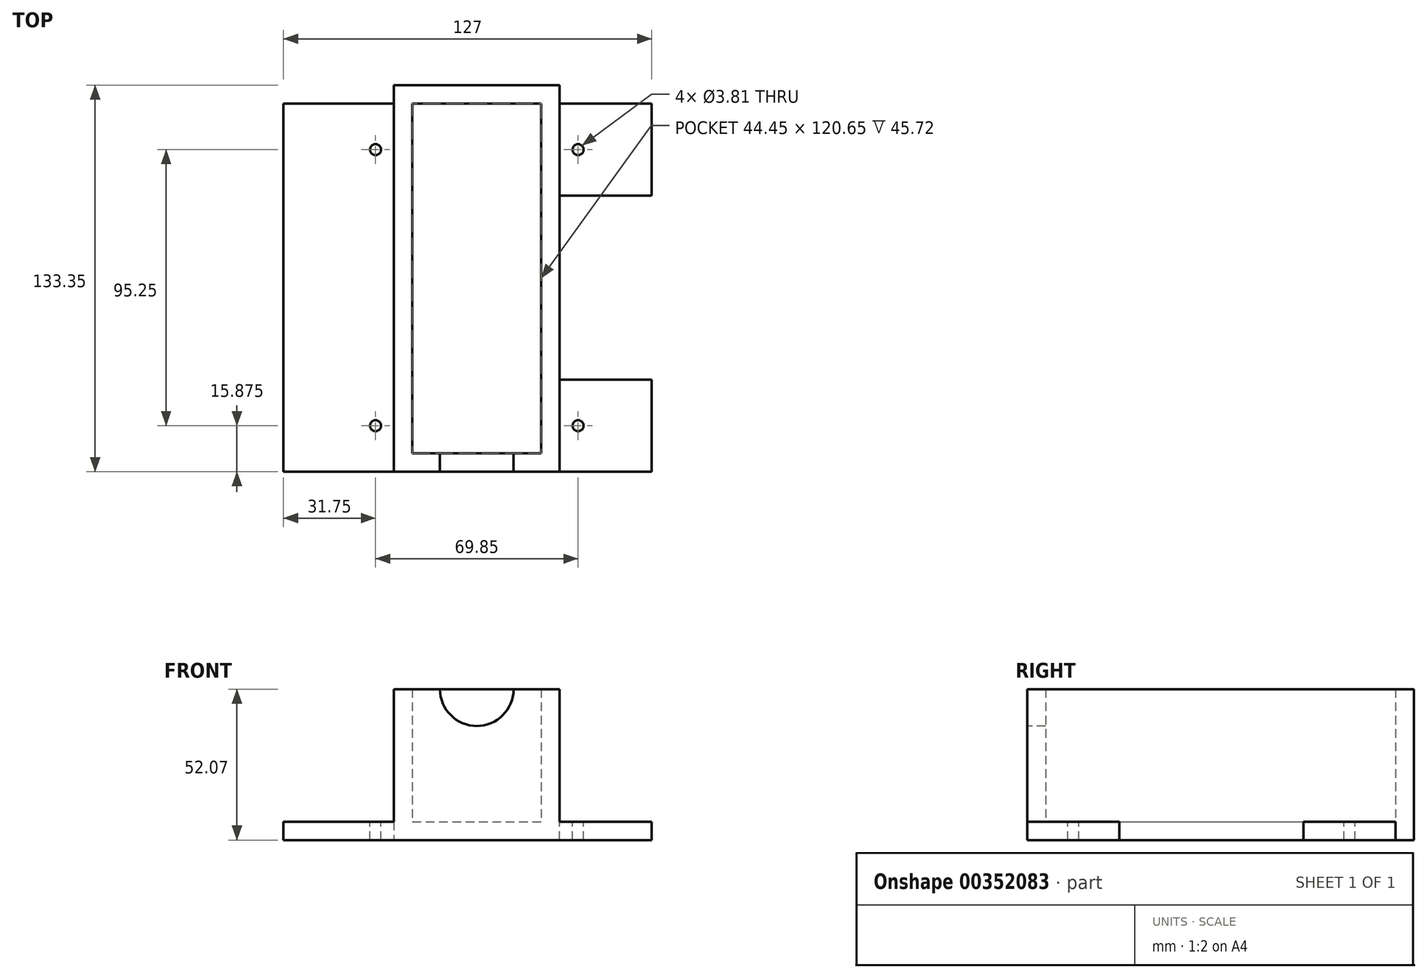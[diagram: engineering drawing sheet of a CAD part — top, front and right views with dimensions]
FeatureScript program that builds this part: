
annotation { "Feature Type Name" : "Feature", "Feature Type Description" : "" }
export const myFeature = defineFeature(function(context is Context, id is Id, definition is map)
    precondition{}
    {
        {
            var Q0;
            Q0=qCreatedBy(makeId("Front.planeOp"),FACE);
            var sketch = newSketch(context, id + "F0", { "sketchPlane" : qUnion([Q0])});
            skLineSegment(sketch, "E0.bottom", {"start": v(-44.45, 45.72) * mm, "end": v(0, 45.72) * mm});
            skLineSegment(sketch, "E0.top", {"start": v(-44.45, 0) * mm, "end": v(0, 0) * mm});
            skLineSegment(sketch, "E0.left", {"start": v(-44.45, 45.72) * mm, "end": v(-44.45, 0) * mm});
            skLineSegment(sketch, "E0.right", {"start": v(0, 45.72) * mm, "end": v(0, 0) * mm});
            skSolve(sketch);
        }
        {
            var Q0;
            Q0 = qSketchRegion(id + "F0", true);
            extrude(context, id + "F1", {"entities" : qUnion([Q0]), "depth" : 120.65 * mm});
        }
        {
            var Q0;
            Q0=makeQuery(id+"F1.opExtrude","SWEPT_FACE",FACE,{"disambiguationData":[OSD([sQuery(id+"F0.wireOp",EDGE,"E0.bottom")])]});
            shell(context, id + "F2", {"entities" : qUnion([Q0]), "thickness" : 6.35 * mm, "oppositeDirection" : true});
        }
        {
            var Q0;
            Q0=qCreatedBy(makeId("Right.planeOp"),FACE);
            var sketch = newSketch(context, id + "F3", { "sketchPlane" : qUnion([Q0])});
            skPoint(sketch, "E1", {"position": v(0, 0) * mm});
            skPoint(sketch, "E2", {"position": v(-31.75, -6.35) * mm});
            skLineSegment(sketch, "E3.bottom", {"start": v(0, 0) * mm, "end": v(-31.75, 0) * mm});
            skLineSegment(sketch, "E3.top", {"start": v(0, -6.35) * mm, "end": v(-31.75, -6.35) * mm});
            skLineSegment(sketch, "E3.left", {"start": v(0, 0) * mm, "end": v(0, -6.35) * mm});
            skLineSegment(sketch, "E3.right", {"start": v(-31.75, 0) * mm, "end": v(-31.75, -6.35) * mm});
            skSolve(sketch);
        }
        {
            var Q0;
            Q0=qCreatedBy(makeId("Front.planeOp"),FACE);
            var sketch = newSketch(context, id + "F4", { "sketchPlane" : qUnion([Q0])});
            skPoint(sketch, "E4", {"position": v(-50.8, 0) * mm});
            skPoint(sketch, "E5", {"position": v(-88.9, -6.35) * mm});
            skLineSegment(sketch, "E6.bottom", {"start": v(-50.8, 0) * mm, "end": v(-88.9, 0) * mm});
            skLineSegment(sketch, "E6.top", {"start": v(-50.8, -6.35) * mm, "end": v(-88.9, -6.35) * mm});
            skLineSegment(sketch, "E6.left", {"start": v(-50.8, 0) * mm, "end": v(-50.8, -6.35) * mm});
            skLineSegment(sketch, "E6.right", {"start": v(-88.9, 0) * mm, "end": v(-88.9, -6.35) * mm});
            skLineSegment(sketch, "E7", {"start": v(0, 0) * mm, "end": v(-50.8, 0) * mm});
            skSolve(sketch);
        }
        {
            var Q0;
            Q0 = qSketchRegion(id + "F4", true);
            extrude(context, id + "F5", {"entities" : qUnion([Q0]), "operationType" : NewBodyOperationType.ADD, "depth" : 127 * mm});
        }
        {
            var Q0;
            Q0=qCreatedBy(makeId("Right.planeOp"),FACE);
            var sketch = newSketch(context, id + "F6", { "sketchPlane" : qUnion([Q0])});
            skPoint(sketch, "E8", {"position": v(-127, 0) * mm});
            skPoint(sketch, "E9", {"position": v(-95.25, -6.35) * mm});
            skLineSegment(sketch, "E10.bottom", {"start": v(-127, 0) * mm, "end": v(-95.25, 0) * mm});
            skLineSegment(sketch, "E10.top", {"start": v(-127, -6.35) * mm, "end": v(-95.25, -6.35) * mm});
            skLineSegment(sketch, "E10.left", {"start": v(-127, 0) * mm, "end": v(-127, -6.35) * mm});
            skLineSegment(sketch, "E10.right", {"start": v(-95.25, 0) * mm, "end": v(-95.25, -6.35) * mm});
            skLineSegment(sketch, "E11", {"start": v(-95.25, 0) * mm, "end": v(0, 0) * mm});
            skSolve(sketch);
        }
        {
            var Q0;
            Q0 = qSketchRegion(id + "F6", true);
            extrude(context, id + "F7", {"entities" : qUnion([Q0]), "operationType" : NewBodyOperationType.ADD, "depth" : 38.1 * mm});
        }
        {
            var Q0;
            Q0 = qSketchRegion(id + "F3", true);
            extrude(context, id + "F8", {"entities" : qUnion([Q0]), "operationType" : NewBodyOperationType.ADD, "depth" : 38.1 * mm});
        }
        {
            var Q0;
            Q0=makeQuery(id+"F5.opExtrude","SWEPT_FACE",FACE,{"disambiguationData":[OSD([sQuery(id+"F4.wireOp",EDGE,"E6.bottom")])]});
            var sketch = newSketch(context, id + "F9", { "sketchPlane" : qUnion([Q0])});
            skCircle(sketch, "E12", {"center": v(-57.15, -111.12) * mm, "radius": 1.9 * mm});
            skLineSegment(sketch, "E13", {"start": v(-57.15, -111.12) * mm, "end": v(-50.8, -111.12) * mm});
            skLineSegment(sketch, "E14", {"start": v(-57.15, -111.12) * mm, "end": v(-57.15, -127) * mm});
            skSolve(sketch);
        }
        {
            var Q0;
            Q0=sQuery(id+"F9.wireOp",VERTEX,"E13.start");
            var Q1;
            Q1=makeQuery(id+"F1.opExtrude","SWEPT_BODY",BODY,{"disambiguationData":[OSD([sQuery(id+"F0.wireOp",EDGE,"E0.bottom"),sQuery(id+"F0.wireOp",EDGE,"E0.top"),sQuery(id+"F0.wireOp",EDGE,"E0.left"),sQuery(id+"F0.wireOp",EDGE,"E0.right")])]});
            hole(context, id + "F10", {"style" : HoleStyle.SIMPLE, "endStyle" : HoleEndStyle.THROUGH, "holeDiameter" : 3.8 * mm, "isTappedThrough" : true, "tappedDepth" : 12.7 * mm, "tapClearance" : 3, "locations" : qUnion([Q0]), "scope" : qUnion([Q1])});
        }
        {
            var Q0;
            Q0=makeQuery(id+"F5.opExtrude","SWEPT_FACE",FACE,{"disambiguationData":[OSD([sQuery(id+"F4.wireOp",EDGE,"E6.bottom")])]});
            var sketch = newSketch(context, id + "F11", { "sketchPlane" : qUnion([Q0])});
            skCircle(sketch, "E15", {"center": v(-57.15, -15.87) * mm, "radius": 1.9 * mm});
            skLineSegment(sketch, "E16", {"start": v(-57.15, -15.87) * mm, "end": v(-50.8, -15.87) * mm});
            skLineSegment(sketch, "E17", {"start": v(-57.15, -15.87) * mm, "end": v(-57.15, 0) * mm});
            skSolve(sketch);
        }
        {
            var Q0;
            Q0=sQuery(id+"F11.wireOp",VERTEX,"E15.center");
            var Q1;
            Q1=makeQuery(id+"F1.opExtrude","SWEPT_BODY",BODY,{"disambiguationData":[OSD([sQuery(id+"F0.wireOp",EDGE,"E0.bottom"),sQuery(id+"F0.wireOp",EDGE,"E0.top"),sQuery(id+"F0.wireOp",EDGE,"E0.left"),sQuery(id+"F0.wireOp",EDGE,"E0.right")])]});
            hole(context, id + "F12", {"style" : HoleStyle.SIMPLE, "endStyle" : HoleEndStyle.THROUGH, "holeDiameter" : 3.8 * mm, "isTappedThrough" : true, "tappedDepth" : 12.7 * mm, "tapClearance" : 3, "locations" : qUnion([Q0]), "scope" : qUnion([Q1])});
        }
        {
            var Q0;
            Q0=makeQuery(id+"F7.opExtrude","SWEPT_FACE",FACE,{"disambiguationData":[OSD([sQuery(id+"F6.wireOp",EDGE,"E10.bottom")])]});
            var sketch = newSketch(context, id + "F13", { "sketchPlane" : qUnion([Q0])});
            skCircle(sketch, "E18", {"center": v(12.7, -111.13) * mm, "radius": 1.9 * mm});
            skLineSegment(sketch, "E19", {"start": v(12.7, -111.13) * mm, "end": v(6.35, -111.13) * mm});
            skLineSegment(sketch, "E20", {"start": v(12.7, -111.13) * mm, "end": v(12.7, -95.25) * mm});
            skSolve(sketch);
        }
        {
            var Q0;
            Q0=sQuery(id+"F13.wireOp",VERTEX,"E18.center");
            var Q1;
            Q1=makeQuery(id+"F1.opExtrude","SWEPT_BODY",BODY,{"disambiguationData":[OSD([sQuery(id+"F0.wireOp",EDGE,"E0.bottom"),sQuery(id+"F0.wireOp",EDGE,"E0.top"),sQuery(id+"F0.wireOp",EDGE,"E0.left"),sQuery(id+"F0.wireOp",EDGE,"E0.right")])]});
            hole(context, id + "F14", {"style" : HoleStyle.SIMPLE, "endStyle" : HoleEndStyle.THROUGH, "holeDiameter" : 3.8 * mm, "isTappedThrough" : true, "tappedDepth" : 12.7 * mm, "tapClearance" : 3, "locations" : qUnion([Q0]), "scope" : qUnion([Q1])});
        }
        {
            var Q0;
            Q0=makeQuery(id+"F8.opExtrude","SWEPT_FACE",FACE,{"disambiguationData":[OSD([sQuery(id+"F3.wireOp",EDGE,"E3.bottom")])]});
            var sketch = newSketch(context, id + "F15", { "sketchPlane" : qUnion([Q0])});
            skCircle(sketch, "E21", {"center": v(12.7, -15.87) * mm, "radius": 1.9 * mm});
            skLineSegment(sketch, "E22", {"start": v(6.35, -15.87) * mm, "end": v(12.7, -15.87) * mm});
            skLineSegment(sketch, "E23", {"start": v(12.7, -15.87) * mm, "end": v(12.7, 0) * mm});
            skSolve(sketch);
        }
        {
            var Q0;
            Q0=sQuery(id+"F15.wireOp",VERTEX,"E22.end");
            var Q1;
            Q1=makeQuery(id+"F1.opExtrude","SWEPT_BODY",BODY,{"disambiguationData":[OSD([sQuery(id+"F0.wireOp",EDGE,"E0.bottom"),sQuery(id+"F0.wireOp",EDGE,"E0.top"),sQuery(id+"F0.wireOp",EDGE,"E0.left"),sQuery(id+"F0.wireOp",EDGE,"E0.right")])]});
            hole(context, id + "F16", {"style" : HoleStyle.SIMPLE, "endStyle" : HoleEndStyle.THROUGH, "holeDiameter" : 3.8 * mm, "isTappedThrough" : true, "tappedDepth" : 12.7 * mm, "tapClearance" : 3, "locations" : qUnion([Q0]), "scope" : qUnion([Q1])});
        }
        {
            var Q0;
            Q0=makeQuery(id+"F7.boolean.opBoolean","MERGE",FACE,{"derivedFrom":[makeQuery(id+"F5.boolean.opBoolean","MERGE",FACE,{"derivedFrom":[makeQuery(id+"F1.opExtrude","CAP_FACE",FACE,{"disambiguationData":[OSD([sQuery(id+"F0.wireOp",EDGE,"E0.bottom"),sQuery(id+"F0.wireOp",EDGE,"E0.top"),sQuery(id+"F0.wireOp",EDGE,"E0.left"),sQuery(id+"F0.wireOp",EDGE,"E0.right")])],"isStart":false}),makeQuery(id+"F5.opExtrude","CAP_FACE",FACE,{"disambiguationData":[OSD([sQuery(id+"F4.wireOp",EDGE,"E6.bottom"),sQuery(id+"F4.wireOp",EDGE,"E6.top"),sQuery(id+"F4.wireOp",EDGE,"E6.left"),sQuery(id+"F4.wireOp",EDGE,"E6.right")])],"isStart":false})]}),makeQuery(id+"F7.opExtrude","SWEPT_FACE",FACE,{"disambiguationData":[OSD([sQuery(id+"F6.wireOp",EDGE,"E10.left")])]})]});
            var sketch = newSketch(context, id + "F17", { "sketchPlane" : qUnion([Q0])});
            skCircle(sketch, "E24", {"center": v(-22.23, 45.72) * mm, "radius": 12.7 * mm});
            skSolve(sketch);
        }
        {
            var Q0;
            Q0=sQuery(id+"F17.wireOp",VERTEX,"E24.center");
            var Q1;
            Q1=makeQuery(id+"F1.opExtrude","SWEPT_BODY",BODY,{"disambiguationData":[OSD([sQuery(id+"F0.wireOp",EDGE,"E0.bottom"),sQuery(id+"F0.wireOp",EDGE,"E0.top"),sQuery(id+"F0.wireOp",EDGE,"E0.left"),sQuery(id+"F0.wireOp",EDGE,"E0.right")])]});
            hole(context, id + "F18", {"style" : HoleStyle.SIMPLE, "endStyle" : HoleEndStyle.BLIND, "holeDiameter" : 25.4 * mm, "holeDepth" : 15.1 * mm, "isTappedThrough" : true, "tappedDepth" : 12.7 * mm, "tapClearance" : 3, "locations" : qUnion([Q0]), "scope" : qUnion([Q1])});
        }
    });
